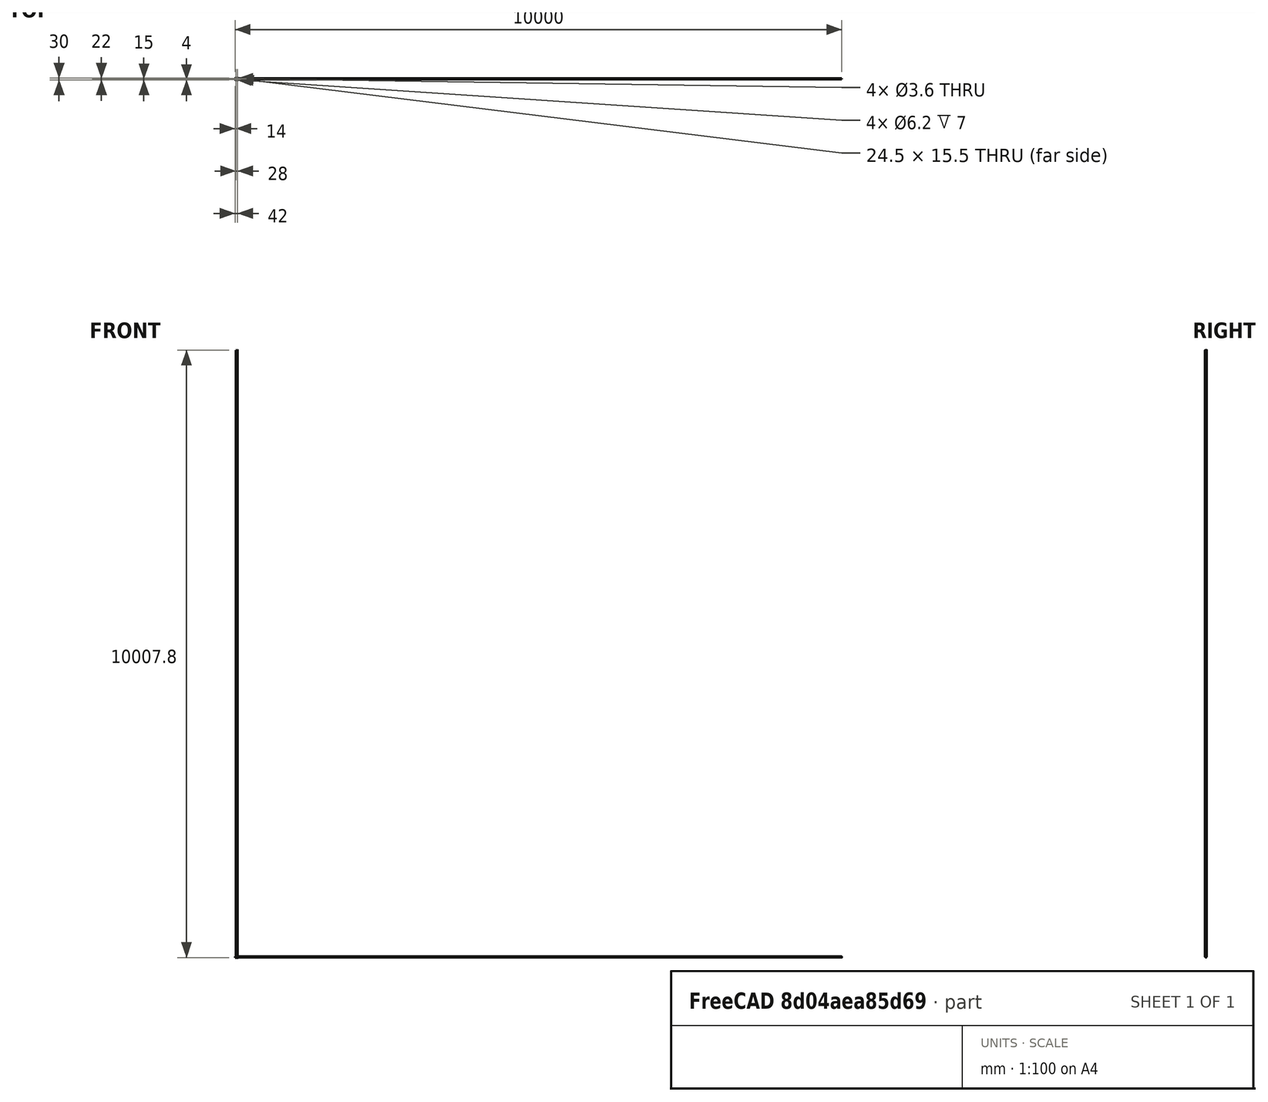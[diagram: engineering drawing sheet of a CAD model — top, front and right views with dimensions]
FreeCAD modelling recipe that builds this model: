
FCSTD DOCUMENT  (FreeCAD 0.15R4671 (Git))
Label: 2xBearingCap
License: All rights reserved
LicenseURL: http://en.wikipedia.org/wiki/All_rights_reserved
objects: Sketcher::SketchObject×9, PartDesign::Pocket×6, Mesh::Feature×4, Part::Feature×3, PartDesign::Pad×3, PartDesign::Fillet×2
note: 32 computed .brp shape members not serialized (recipe doc carries the construction recipe); baked Part::Feature solids carry a one-line shape summary decoded from their .brp

FEATURE [Part::Feature] LM8UU_8mm_Linear_Bearing
  shape: bbox 24 x 15 x 15 mm, 34 faces (baked)
FEATURE [Part::Feature] LM8UU_8mm_Linear_Bearing001
  Placement = pos=(28,0,0) rot=(0,0,1;0rad)
  shape: bbox 24 x 15 x 15 mm, 34 faces (baked)
FEATURE [Sketcher::SketchObject] Sketch
  sketch-geometry (4):
    g0: LineSegment StartX=-2 StartY=-15 StartZ=0 EndX=54 EndY=-15 EndZ=0
    g1: LineSegment StartX=54 StartY=-15 StartZ=0 EndX=54 EndY=15 EndZ=0
    g2: LineSegment StartX=54 StartY=15 StartZ=0 EndX=-2 EndY=15 EndZ=0
    g3: LineSegment StartX=-2 StartY=15 StartZ=0 EndX=-2 EndY=-15 EndZ=0
  constraints (8):
    c: Coincident(g0,g1)
    c: Coincident(g1,g2)
    c: Coincident(g2,g3)
    c: Coincident(g3,g0)
    c: Horizontal(g0)
    c: Horizontal(g2)
    c: Vertical(g1)
    c: Vertical(g3)
FEATURE [PartDesign::Pad] Pad
  Length = 9
  Length2 = 100
  Sketch = -> Sketch
  Type = 0
FEATURE [Sketcher::SketchObject] Sketch001
  Placement = pos=(-2,0,0) rot=(0.57735,-0.57735,-0.57735;2.0944rad)
  Support = -> Pad [Face4]
  sketch-geometry (1):
    g0: Circle CenterX=0 CenterY=0 CenterZ=0 NormalX=0 NormalY=0 NormalZ=1 Radius=7.75
  constraints (2):
    c: Coincident(g0,g-1)
    c: Radius(g0) = 7.75
FEATURE [PartDesign::Pocket] Pocket
  Length = 26.25
  Sketch = -> Sketch001
  Type = 0
FEATURE [Sketcher::SketchObject] Sketch002
  Placement = pos=(54,0,0) rot=(0.57735,0.57735,0.57735;2.0944rad)
  Support = -> Pocket [Face3]
  sketch-geometry (1):
    g0: Circle CenterX=0 CenterY=0 CenterZ=0 NormalX=0 NormalY=0 NormalZ=1 Radius=7.75
  constraints (2):
    c: Coincident(g0,g-1)
    c: Radius(g0) = 7.75
FEATURE [PartDesign::Pocket] Pocket001
  Length = 26.25
  Sketch = -> Sketch002
  Type = 0
FEATURE [Sketcher::SketchObject] Sketch003
  Placement = pos=(54,0,0) rot=(0.57735,0.57735,0.57735;2.0944rad)
  Support = -> Pocket001 [Face3]
  sketch-geometry (2):
    g0: ArcOfCircle CenterX=0 CenterY=0 CenterZ=0 NormalX=0 NormalY=0 NormalZ=1 Radius=8 StartAngle=0 EndAngle=3.14159
    g1: LineSegment StartX=-8 StartY=0 StartZ=0 EndX=8 EndY=0 EndZ=0
  constraints (3):
    c: Coincident(g1,g0)
    c: Coincident(g1,g0)
    c: Horizontal(g1)
FEATURE [PartDesign::Pad] Pad001
  Length = 1.75
  Length2 = 100
  Reversed = true
  Sketch = -> Sketch003
  Type = 0
FEATURE [Sketcher::SketchObject] Sketch004
  Placement = pos=(-2,0,0) rot=(0.57735,-0.57735,-0.57735;2.0944rad)
  Support = -> Pad001 [Face2]
  sketch-geometry (2):
    g0: ArcOfCircle CenterX=0 CenterY=0 CenterZ=0 NormalX=0 NormalY=0 NormalZ=1 Radius=8 StartAngle=0 EndAngle=3.14159
    g1: LineSegment StartX=-8 StartY=0 StartZ=0 EndX=8 EndY=0 EndZ=0
  constraints (5):
    c: Coincident(g0,g-1)
    c: PointOnObject(g0,g-1)
    c: PointOnObject(g0,g-1)
    c: Coincident(g1,g0)
    c: Coincident(g1,g0)
FEATURE [PartDesign::Pad] Pad002
  Length = 1.75
  Length2 = 100
  Reversed = true
  Sketch = -> Sketch004
  Type = 0
FEATURE [Sketcher::SketchObject] Sketch005
  Placement = pos=(-2,0,0) rot=(0.57735,-0.57735,-0.57735;2.0944rad)
  Support = -> Pad002 [Face5]
  sketch-geometry (1):
    g0: Circle CenterX=0 CenterY=0 CenterZ=0 NormalX=0 NormalY=0 NormalZ=1 Radius=6.5
  constraints (1):
    c: Radius(g0) = 6.5
FEATURE [PartDesign::Pocket] Pocket002
  Length = 5
  Sketch = -> Sketch005
  Type = 1
FEATURE [Mesh::Feature] SocketHeadCapScrew_M3x008  label="SocketHeadCapScrew_M3x019"
  Placement = pos=(20,21,-113) rot=(0,0,1;0rad)
FEATURE [Mesh::Feature] SocketHeadCapScrew_M3x009  label="SocketHeadCapScrew_M3x020"
  Placement = pos=(48,21,-113) rot=(0,0,1;0rad)
FEATURE [Mesh::Feature] SocketHeadCapScrew_M3x011  label="SocketHeadCapScrew_M3x016"
  Placement = pos=(20,-1,-113) rot=(0,0,1;0rad)
FEATURE [Mesh::Feature] SocketHeadCapScrew_M3x012  label="SocketHeadCapScrew_M3x017"
  Placement = pos=(48,-1,-113) rot=(0,0,1;0rad)
FEATURE [Sketcher::SketchObject] Sketch006
  Placement = pos=(0,0,0) rot=(1,0,0;3.14159rad)
  Support = -> Pocket002 [Face4]
  sketch-geometry (4):
    g0: Circle CenterX=12 CenterY=11 CenterZ=0 NormalX=0 NormalY=0 NormalZ=1 Radius=1.8
    g1: Circle CenterX=12 CenterY=-11 CenterZ=0 NormalX=0 NormalY=0 NormalZ=1 Radius=1.8
    g2: Circle CenterX=40 CenterY=11 CenterZ=0 NormalX=0 NormalY=0 NormalZ=1 Radius=1.8
    g3: Circle CenterX=40 CenterY=-11 CenterZ=0 NormalX=0 NormalY=0 NormalZ=1 Radius=1.8
  constraints (4):
    c: Radius(g0) = 1.8
    c: Radius(g1) = 1.8
    c: Radius(g2) = 1.8
    c: Radius(g3) = 1.8
FEATURE [PartDesign::Pocket] Pocket003
  Length = 5
  Sketch = -> Sketch006
  Type = 1
FEATURE [Sketcher::SketchObject] Sketch007
  Placement = pos=(0,0,9) rot=(0,0,1;0rad)
  Support = -> Pocket003 [Face5]
  sketch-geometry (4):
    g0: Circle CenterX=12 CenterY=-11 CenterZ=0 NormalX=0 NormalY=0 NormalZ=1 Radius=3.1
    g1: Circle CenterX=40 CenterY=-11 CenterZ=0 NormalX=0 NormalY=0 NormalZ=1 Radius=3.1
    g2: Circle CenterX=12 CenterY=11 CenterZ=0 NormalX=0 NormalY=0 NormalZ=1 Radius=3.1
    g3: Circle CenterX=40 CenterY=11 CenterZ=0 NormalX=0 NormalY=0 NormalZ=1 Radius=3.1
  constraints (4):
    c: Radius(g2) = 3.1
    c: Radius(g3) = 3.1
    c: Radius(g1) = 3.1
    c: Radius(g0) = 3.1
FEATURE [PartDesign::Pocket] Pocket004
  Length = 7
  Sketch = -> Sketch007
  Type = 0
FEATURE [Sketcher::SketchObject] Sketch008
  Placement = pos=(0,0,0) rot=(1,0,0;3.14159rad)
  Support = -> Pocket004 [Face4]
  sketch-geometry (16):
    g0: ArcOfCircle CenterX=12 CenterY=11 CenterZ=0 NormalX=0 NormalY=0 NormalZ=1 Radius=4 StartAngle=0 EndAngle=3.14159
    g1: ArcOfCircle CenterX=40 CenterY=11 CenterZ=0 NormalX=0 NormalY=0 NormalZ=1 Radius=4 StartAngle=0 EndAngle=3.14159
    g2: ArcOfCircle CenterX=40 CenterY=-11 CenterZ=0 NormalX=0 NormalY=0 NormalZ=1 Radius=4 StartAngle=3.14159 EndAngle=6.28319
    g3: ArcOfCircle CenterX=12 CenterY=-11 CenterZ=0 NormalX=0 NormalY=0 NormalZ=1 Radius=4 StartAngle=3.14159 EndAngle=6.28319
    g4: LineSegment StartX=-3 StartY=-11 StartZ=0 EndX=-3 EndY=-17 EndZ=0
    g5: LineSegment StartX=-3 StartY=-17 StartZ=0 EndX=55 EndY=-17 EndZ=0
    g6: LineSegment StartX=55 StartY=-17 StartZ=0 EndX=55 EndY=-11 EndZ=0
    g7: LineSegment StartX=55 StartY=-11 StartZ=0 EndX=44 EndY=-11 EndZ=0
    g8: LineSegment StartX=36 StartY=-11 StartZ=0 EndX=16 EndY=-11 EndZ=0
    g9: LineSegment StartX=8 StartY=-11 StartZ=0 EndX=-3 EndY=-11 EndZ=0
    g10: LineSegment StartX=36 StartY=11 StartZ=0 EndX=16 EndY=11 EndZ=0
    g11: LineSegment StartX=8 StartY=11 StartZ=0 EndX=-3 EndY=11 EndZ=0
    g12: LineSegment StartX=-3 StartY=11 StartZ=0 EndX=-3 EndY=17 EndZ=0
    g13: LineSegment StartX=-3 StartY=17 StartZ=0 EndX=55 EndY=17 EndZ=0
    g14: LineSegment StartX=55 StartY=17 StartZ=0 EndX=55 EndY=11 EndZ=0
    g15: LineSegment StartX=55 StartY=11 StartZ=0 EndX=44 EndY=11 EndZ=0
  constraints (27):
    c: Vertical(g4)
    c: Coincident(g4,g5)
    c: Horizontal(g5)
    c: Coincident(g5,g6)
    c: Vertical(g6)
    c: Coincident(g7,g6)
    c: Coincident(g7,g2)
    c: Horizontal(g7)
    c: Coincident(g8,g2)
    c: Coincident(g8,g3)
    c: Horizontal(g8)
    c: Coincident(g9,g3)
    c: Coincident(g9,g4)
    c: Horizontal(g9)
    c: Coincident(g10,g1)
    c: Coincident(g10,g0)
    c: Horizontal(g10)
    c: Coincident(g0,g11)
    c: Coincident(g11,g12)
    c: Vertical(g12)
    c: Coincident(g12,g13)
    c: Horizontal(g13)
    c: Coincident(g13,g14)
    c: Vertical(g14)
    c: Coincident(g14,g15)
    c: Coincident(g15,g1)
    c: Horizontal(g15)
FEATURE [PartDesign::Pocket] Pocket005
  Length = 5
  Sketch = -> Sketch008
  Type = 1
FEATURE [PartDesign::Fillet] Fillet
  Base = -> Pocket005 [Edge76,Edge75,Edge48,Edge53]
  Radius = 4
FEATURE [PartDesign::Fillet] Fillet001
  Base = -> Fillet [Edge42,Edge30,Edge37,Edge24,Edge97,Edge99,Edge100,Edge98]
  Radius = 2
FEATURE [Part::Feature] Fillet001001  label="2xBearingCap"
  shape: bbox 56 x 30 x 9 mm, 48 faces (baked)
